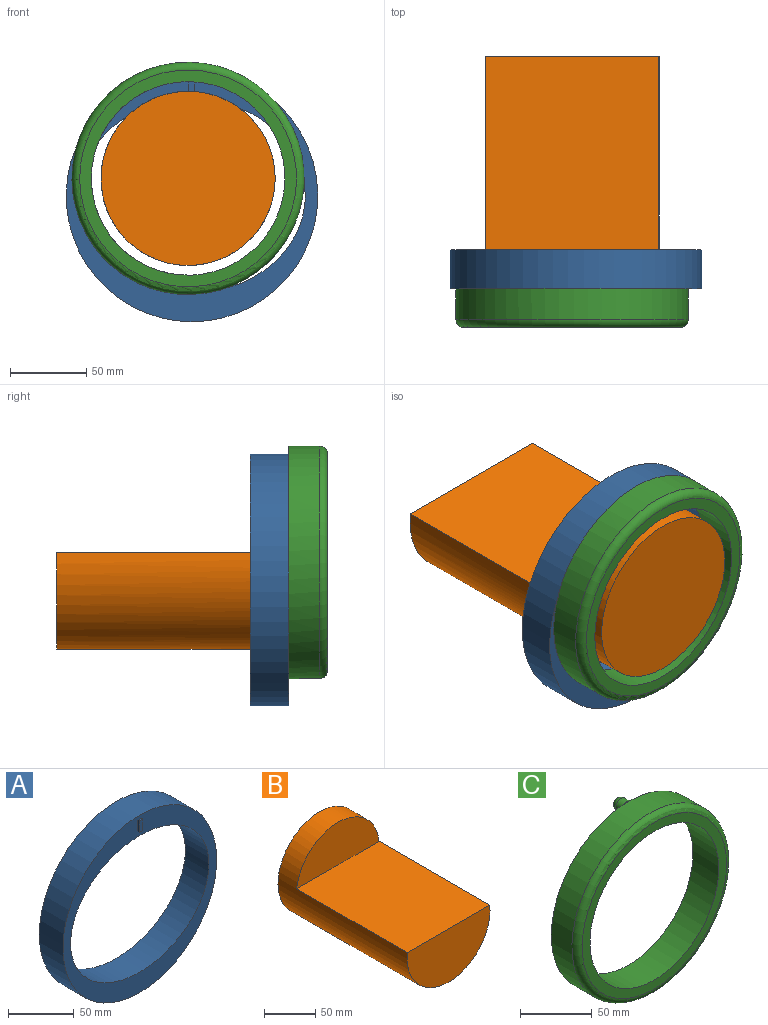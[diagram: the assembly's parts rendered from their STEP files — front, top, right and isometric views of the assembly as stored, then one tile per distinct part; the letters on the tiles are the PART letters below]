
ASSEMBLY  parts=3 mates=4
PART A: 9 faces, bbox 165.1x26.7x165.1 mm
  f0: plane 165.1x165.1mm, normal (0,-1,0), area 6547mm2, adj f1,f2,f4,f5,f6,f7
  f1: extruded ~148.59x127mm, area 11012.4mm2, adj f0,f3
  f2: cylinder r=82.55mm len=165.1mm, axis (0,1,0), area 13174.4mm2, adj f0,f3
  f3: plane 165.1x165.1mm, normal (0,1,0), area 6587.2mm2, adj f1,f2
  f4: plane 3.66x1.27mm, normal (0,0,1), area 4.7mm2, adj f0,f5,f7,f8
  f5: plane 10.99x1.27mm, normal (-1,0,0), area 14mm2, adj f0,f4,f6,f8
  f6: plane 3.66x1.27mm, normal (0,0,-1), area 4.7mm2, adj f0,f5,f7,f8
  f7: plane 10.99x1.27mm, normal (1,0,0), area 14mm2, adj f0,f4,f6,f8
  f8: plane 10.99x3.66mm, normal (0,-1,0), area 40.2mm2, adj f4,f5,f6,f7
PART B: 5 faces, bbox 114.3x177.8x114.3 mm
  f0: cylinder r=57.15mm len=177.8mm, axis (0,1,0), area 38422.4mm2, adj f1,f2,f3,f4
  f1: plane 114.3x63.5mm, normal (0,-1,0), area 5854.7mm2, adj f0,f4
  f2: plane 114.3x114.3mm, normal (0,1,0), area 10260.8mm2, adj f0
  f3: plane 113.59x50.8mm, normal (0,-1,0), area 4406.1mm2, adj f0,f4
  f4: plane 152.4x113.59mm, normal (0,0,1), area 17311.5mm2, adj f0,f1,f3
PART C: 11 faces, bbox 165x38.1x165 mm
  f0: cylinder r=63.5mm len=127mm, axis (0,1,0), area 10134.1mm2, adj f2,f3,f6
  f1: cylinder r=76.2mm len=152.4mm, axis (0,1,0), area 9728.8mm2, adj f3,f9,f10
  f2: plane 142.24x142.24mm, normal (0,-1,0), area 3222.7mm2, adj f0,f10
  f3: plane 152.4x152.33mm, normal (0,1,0), area 5421.5mm2, adj f0,f1,f7,f8
  f4: cylinder r=5.08mm len=10.16mm, axis (0,-1,0), area 178.7mm2, adj f5,f6,f7,f8,f9
  f5: sphere r=5.08mm, area 162.1mm2, adj f4
  f6: bspline ~6.11x2.03mm, area 13.3mm2, adj f0,f4,f7,f8
  f7: torus R=7.11mm, axis (0,-1,0), area 41mm2, adj f3,f4,f6,f9
  f8: torus R=7.11mm, axis (0,-1,0), area 41mm2, adj f3,f4,f6,f9
  f9: bspline ~7.62x2.33mm, area 14.7mm2, adj f1,f4,f7,f8
  f10: torus R=71.12mm, axis (0,-1,0), area 3727.9mm2, adj f1,f2
PLACE A rot(axis=(0,-1,0),0deg) t=(5.51,28.25,3.91)mm
PLACE B rot(axis=(0,0,-1),180deg) t=(2.94,-22.55,15.41)mm fixed
PLACE C rot(axis=(0,-1,0),179.3deg) t=(2.94,2.85,15.41)mm
MATE planar A.f0 <-> C.f3  axis (0,-1,0) through (5.51,2.85,3.46)mm
MATE parallel A.f4 <-> B.f4  axis (0,0,1) through (5.27,2.21,82.83)mm
MATE revolute B.f0 <-> C.f0  axis (0,-1,0) through (2.94,-22.55,15.41)mm
MATE planar B.f0 <-> C.f1  axis (0,-1,0) through (2.94,-22.55,15.41)mm
